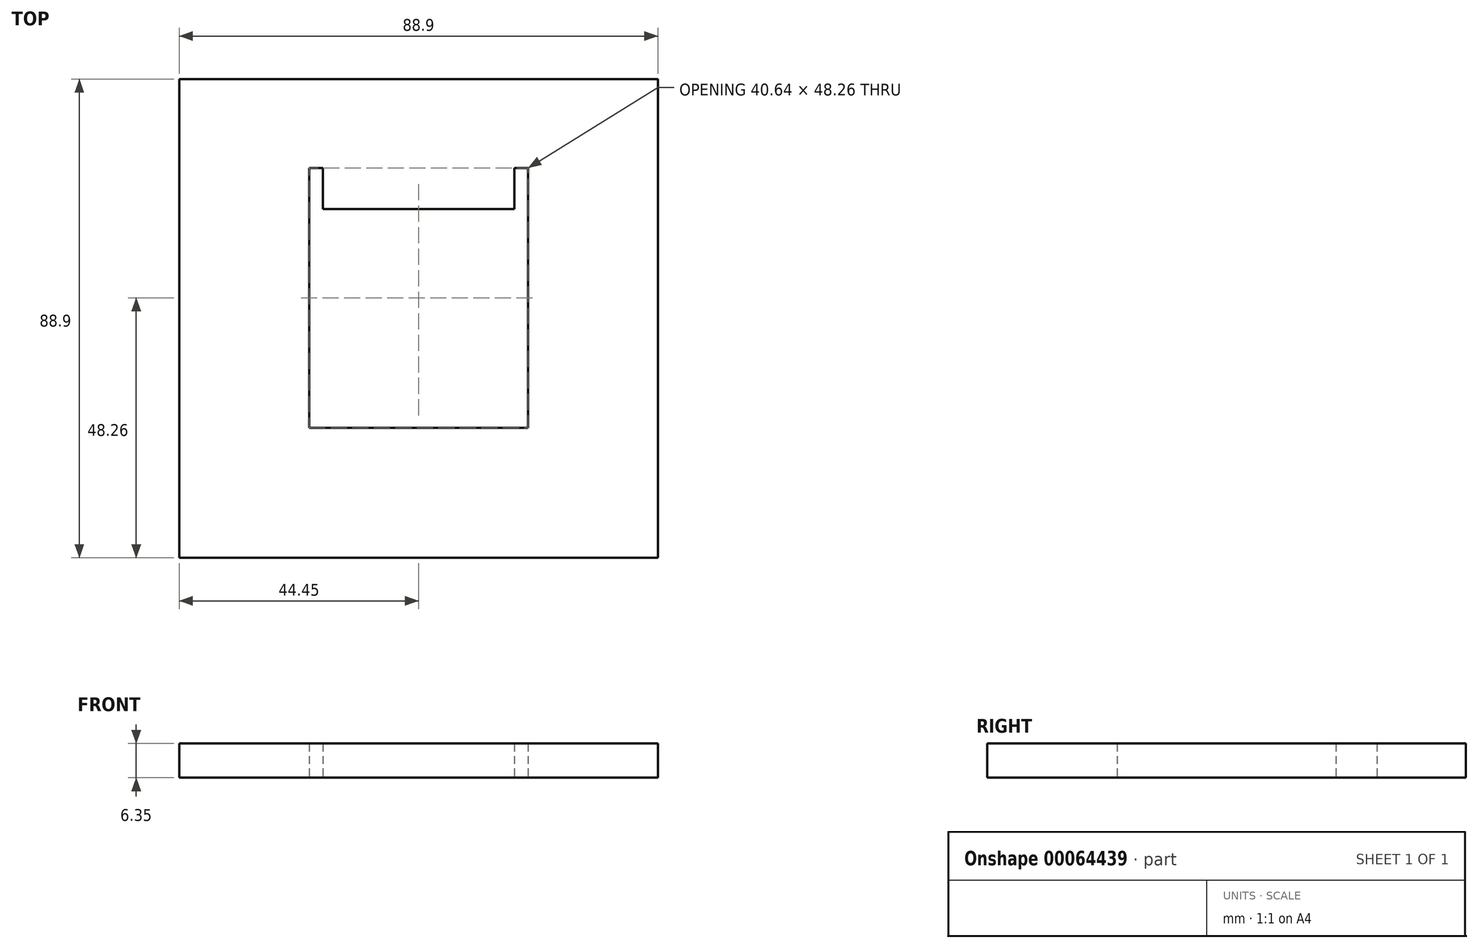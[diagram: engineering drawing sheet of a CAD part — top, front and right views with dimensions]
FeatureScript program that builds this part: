
annotation { "Feature Type Name" : "Feature", "Feature Type Description" : "" }
export const myFeature = defineFeature(function(context is Context, id is Id, definition is map)
    precondition{}
    {
        {
            var Q0;
            Q0=qCreatedBy(makeId("Top.planeOp"),FACE);
            var sketch = newSketch(context, id + "F0", { "sketchPlane" : qUnion([Q0])});
            skLineSegment(sketch, "E0.rect.bottom", {"start": v(44.45, 44.45) * mm, "end": v(-44.45, 44.45) * mm});
            skLineSegment(sketch, "E0.rect.top", {"start": v(44.45, -44.45) * mm, "end": v(-44.45, -44.45) * mm});
            skLineSegment(sketch, "E0.rect.left", {"start": v(44.45, 44.45) * mm, "end": v(44.45, -44.45) * mm});
            skLineSegment(sketch, "E0.rect.right", {"start": v(-44.45, 44.45) * mm, "end": v(-44.45, -44.45) * mm});
            skPoint(sketch, "E0.rect.middle", {"position": v(0, 0) * mm});
            skLineSegment(sketch, "E1.rect.bottom", {"start": v(-17.78, 20.32) * mm, "end": v(17.78, 20.32) * mm});
            skLineSegment(sketch, "E1.rect.top", {"start": v(-20.32, -20.32) * mm, "end": v(20.32, -20.32) * mm});
            skLineSegment(sketch, "E1.rect.left", {"start": v(-20.32, 20.32) * mm, "end": v(-20.32, -20.32) * mm});
            skLineSegment(sketch, "E1.rect.right", {"start": v(20.32, 20.32) * mm, "end": v(20.32, -20.32) * mm});
            skLineSegment(sketch, "E2.top", {"start": v(-20.32, 27.94) * mm, "end": v(-17.78, 27.94) * mm});
            skLineSegment(sketch, "E2.left", {"start": v(-20.32, 20.32) * mm, "end": v(-20.32, 27.94) * mm});
            skLineSegment(sketch, "E2.right", {"start": v(-17.78, 20.32) * mm, "end": v(-17.78, 27.94) * mm});
            skLineSegment(sketch, "E3.top", {"start": v(20.32, 27.94) * mm, "end": v(17.78, 27.94) * mm});
            skLineSegment(sketch, "E3.left", {"start": v(20.32, 20.32) * mm, "end": v(20.32, 27.94) * mm});
            skLineSegment(sketch, "E3.right", {"start": v(17.78, 20.32) * mm, "end": v(17.78, 27.94) * mm});
            skSolve(sketch);
        }
        {
            var Q0;
            Q0 = qSketchRegion(id + "F0", true);
            extrude(context, id + "F1", {"entities" : qUnion([Q0]), "depth" : 6.35 * mm});
        }
    });
